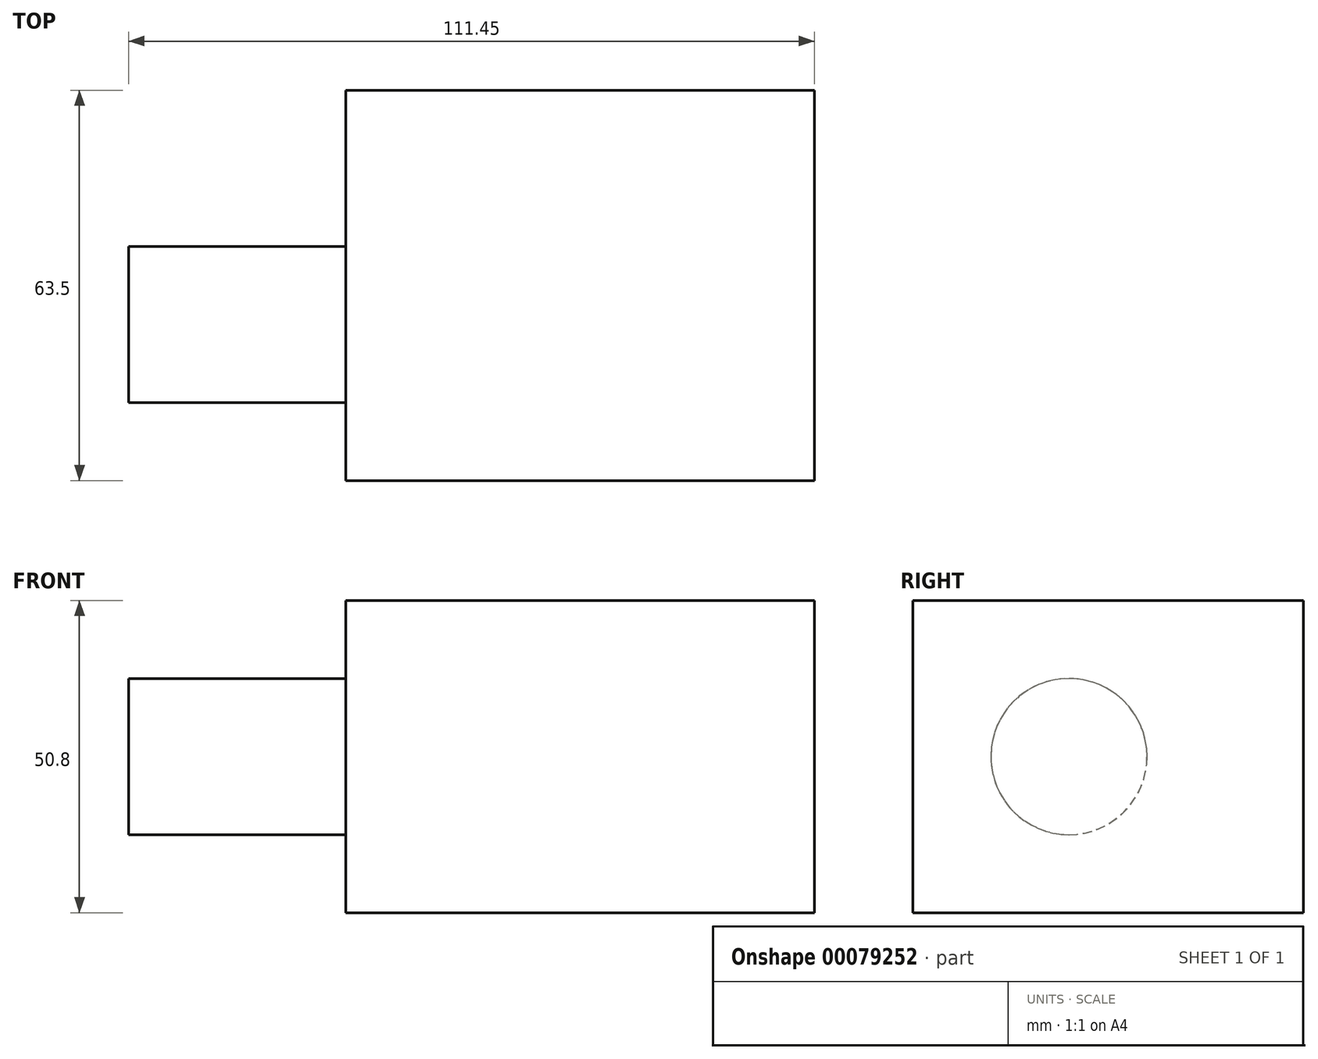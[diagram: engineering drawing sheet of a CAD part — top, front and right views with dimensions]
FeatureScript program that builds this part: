
annotation { "Feature Type Name" : "Feature", "Feature Type Description" : "" }
export const myFeature = defineFeature(function(context is Context, id is Id, definition is map)
    precondition{}
    {
        {
            var Q0;
            Q0=qCreatedBy(makeId("Front.planeOp"),FACE);
            var sketch = newSketch(context, id + "F0", { "sketchPlane" : qUnion([Q0])});
            skLineSegment(sketch, "E0.bottom", {"start": v(0, 0) * mm, "end": v(76.2, 0) * mm});
            skLineSegment(sketch, "E0.top", {"start": v(0, 50.8) * mm, "end": v(76.2, 50.8) * mm});
            skLineSegment(sketch, "E0.left", {"start": v(0, 0) * mm, "end": v(0, 50.8) * mm});
            skLineSegment(sketch, "E0.right", {"start": v(76.2, 0) * mm, "end": v(76.2, 50.8) * mm});
            skSolve(sketch);
        }
        {
            var Q0;
            Q0 = qSketchRegion(id + "F0", true);
            extrude(context, id + "F1", {"entities" : qUnion([Q0]), "depth" : 63.5 * mm});
        }
        {
            var Q0;
            Q0=makeQuery(id+"F1.opExtrude","CAP_FACE",FACE,{"disambiguationData":[OSD([sQuery(id+"F0.wireOp",EDGE,"E0.bottom"),sQuery(id+"F0.wireOp",EDGE,"E0.top"),sQuery(id+"F0.wireOp",EDGE,"E0.left"),sQuery(id+"F0.wireOp",EDGE,"E0.right")])],"isStart":false});
            var sketch = newSketch(context, id + "F2", { "sketchPlane" : qUnion([Q0])});
            skCircle(sketch, "E1", {"center": v(31.75, 31.75) * mm, "radius": 6.35 * mm});
            skSolve(sketch);
        }
        {
            var Q0;
            Q0=makeQuery(id+"F2.imprint","IMPRINT",FACE,{"disambiguationData":[TD([[makeQuery(id+"F2.imprint","IMPRINT",EDGE,{"derivedFrom":sQuery(id+"F2.wireOp",EDGE,"E1")}),1.0]])]});
            extrude(context, id + "F3", {"entities" : qUnion([Q0]), "operationType" : NewBodyOperationType.ADD, "endBound" : BoundingType.UP_TO_NEXT, "oppositeDirection" : true, "depth" : 25.4 * mm});
        }
        {
            var Q0;
            Q0=makeQuery(id+"F1.opExtrude","SWEPT_FACE",FACE,{"disambiguationData":[OSD([sQuery(id+"F0.wireOp",EDGE,"E0.right")])]});
            var sketch = newSketch(context, id + "F4", { "sketchPlane" : qUnion([Q0])});
            skCircle(sketch, "E2", {"center": v(-38.1, 25.4) * mm, "radius": 12.7 * mm});
            skSolve(sketch);
        }
        {
            var Q0;
            Q0 = qSketchRegion(id + "F4", true);
            extrude(context, id + "F5", {"entities" : qUnion([Q0]), "operationType" : NewBodyOperationType.ADD, "endBound" : BoundingType.THROUGH_ALL, "oppositeDirection" : true, "depth" : 25.4 * mm});
        }
    });
